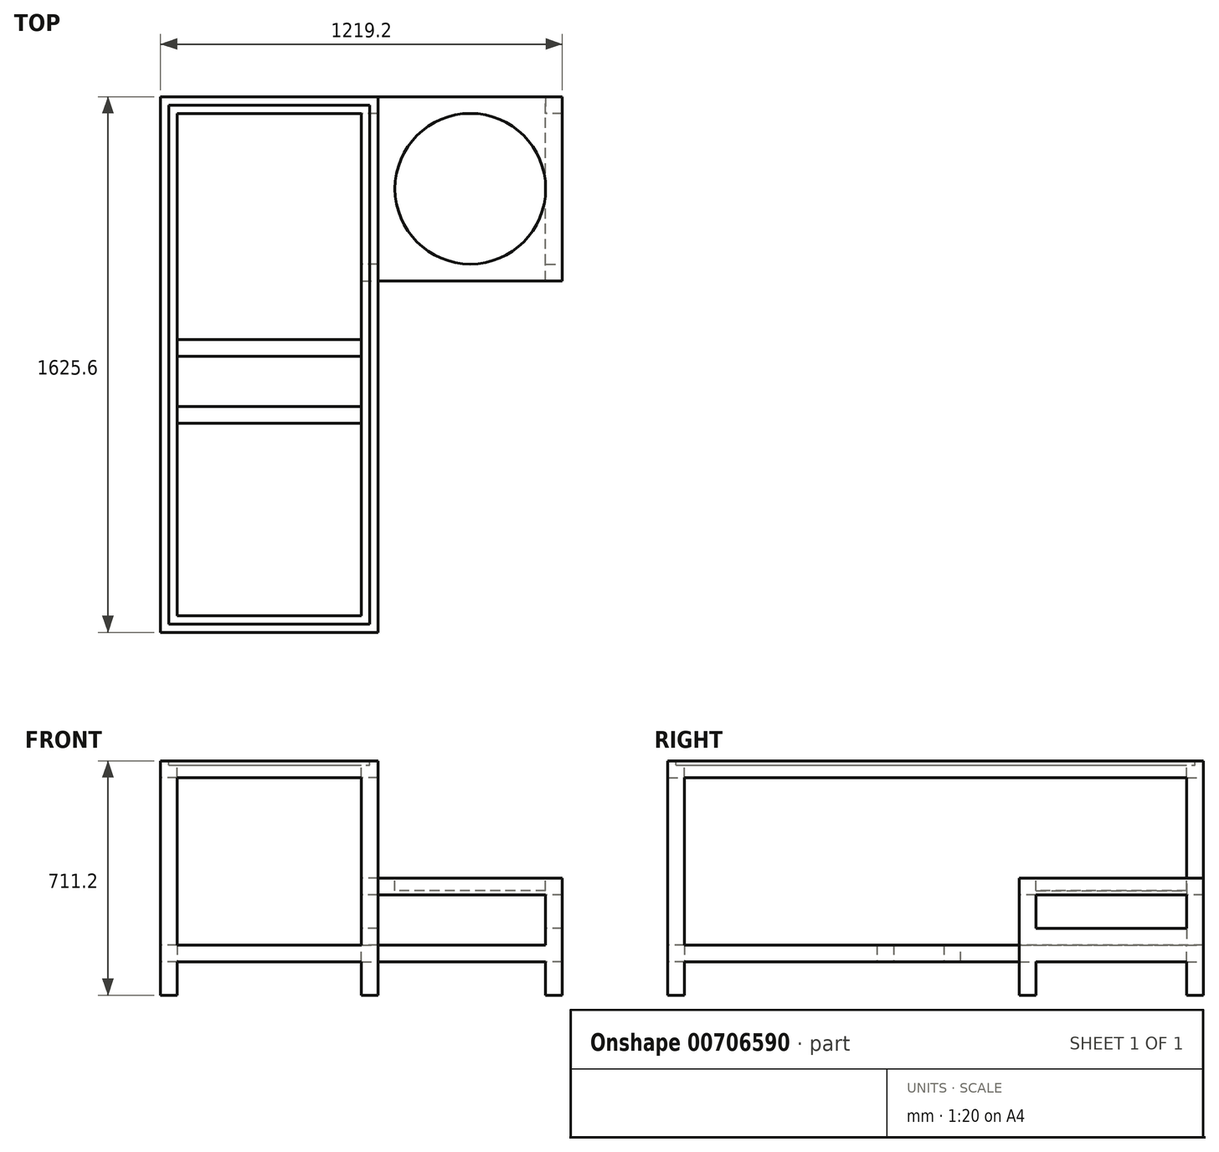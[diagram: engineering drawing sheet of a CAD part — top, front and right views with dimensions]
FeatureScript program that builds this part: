
annotation { "Feature Type Name" : "Feature", "Feature Type Description" : "" }
export const myFeature = defineFeature(function(context is Context, id is Id, definition is map)
    precondition{}
    {
        {
            var Q0;
            Q0=qCreatedBy(makeId("Top.planeOp"),FACE);
            var sketch = newSketch(context, id + "F0", { "sketchPlane" : qUnion([Q0])});
            skLineSegment(sketch, "E0.bottom", {"start": v(-609.6, -762) * mm, "end": v(609.6, -762) * mm});
            skLineSegment(sketch, "E0.top", {"start": v(-609.6, 762) * mm, "end": v(609.6, 762) * mm});
            skLineSegment(sketch, "E0.left", {"start": v(-609.6, -762) * mm, "end": v(-609.6, 762) * mm});
            skLineSegment(sketch, "E0.right", {"start": v(609.6, -762) * mm, "end": v(609.6, 762) * mm});
            skPoint(sketch, "E0.middle", {"position": v(0, 0) * mm});
            skLineSegment(sketch, "E1.0", {"start": v(660.4, -812.8) * mm, "end": v(660.4, 812.8) * mm});
            skLineSegment(sketch, "E1.1", {"start": v(-660.4, -812.8) * mm, "end": v(660.4, -812.8) * mm});
            skLineSegment(sketch, "E1.2", {"start": v(-660.4, -812.8) * mm, "end": v(-660.4, 812.8) * mm});
            skLineSegment(sketch, "E1.3", {"start": v(-660.4, 812.8) * mm, "end": v(660.4, 812.8) * mm});
            skSolve(sketch);
        }
        {
            var Q0;
            Q0=makeQuery(id+"F0.imprint","IMPRINT",FACE,{"disambiguationData":[TD([[makeQuery(id+"F0.imprint","IMPRINT",EDGE,{"derivedFrom":sQuery(id+"F0.wireOp",EDGE,"E0.bottom")}),-1.0]])]});
            extrude(context, id + "F1", {"entities" : qUnion([Q0]), "depth" : 50.8 * mm, "offsetDistance" : 25.4 * mm});
        }
        {
            var Q0;
            Q0=makeQuery(id+"F1.opExtrude","CAP_FACE",FACE,{"disambiguationData":[OSD([sQuery(id+"F0.wireOp",EDGE,"E0.bottom"),sQuery(id+"F0.wireOp",EDGE,"E0.top"),sQuery(id+"F0.wireOp",EDGE,"E0.left"),sQuery(id+"F0.wireOp",EDGE,"E0.right"),sQuery(id+"F0.wireOp",EDGE,"E1.0"),sQuery(id+"F0.wireOp",EDGE,"E1.1"),sQuery(id+"F0.wireOp",EDGE,"E1.2"),sQuery(id+"F0.wireOp",EDGE,"E1.3")])],"isStart":false});
            var sketch = newSketch(context, id + "F2", { "sketchPlane" : qUnion([Q0])});
            skLineSegment(sketch, "E2", {"start": v(-660.4, 812.8) * mm, "end": v(-609.6, 812.8) * mm});
            skLineSegment(sketch, "E3", {"start": v(-609.6, 812.8) * mm, "end": v(-609.6, 762) * mm});
            skLineSegment(sketch, "E4", {"start": v(-609.6, 762) * mm, "end": v(-660.4, 762) * mm});
            skLineSegment(sketch, "E5", {"start": v(-660.4, 762) * mm, "end": v(-660.4, 812.8) * mm});
            skLineSegment(sketch, "E6.MirrorCS", {"start": v(660.4, 812.8) * mm, "end": v(609.6, 812.8) * mm});
            skLineSegment(sketch, "E7.MirrorCS", {"start": v(609.6, 812.8) * mm, "end": v(609.6, 762) * mm});
            skLineSegment(sketch, "E8.MirrorCS", {"start": v(660.4, 762) * mm, "end": v(660.4, 812.8) * mm});
            skLineSegment(sketch, "E9.MirrorCS", {"start": v(609.6, 762) * mm, "end": v(660.4, 762) * mm});
            skLineSegment(sketch, "E10.MirrorCS", {"start": v(609.6, -762) * mm, "end": v(660.4, -762) * mm});
            skLineSegment(sketch, "E11.MirrorCS", {"start": v(-660.4, -812.8) * mm, "end": v(-609.6, -812.8) * mm});
            skLineSegment(sketch, "E12.MirrorCS", {"start": v(-609.6, -812.8) * mm, "end": v(-609.6, -762) * mm});
            skLineSegment(sketch, "E13.MirrorCS", {"start": v(660.4, -762) * mm, "end": v(660.4, -812.8) * mm});
            skLineSegment(sketch, "E14.MirrorCS", {"start": v(-609.6, -762) * mm, "end": v(-660.4, -762) * mm});
            skLineSegment(sketch, "E15.MirrorCS", {"start": v(609.6, -812.8) * mm, "end": v(609.6, -762) * mm});
            skLineSegment(sketch, "E16.MirrorCS", {"start": v(660.4, -812.8) * mm, "end": v(609.6, -812.8) * mm});
            skLineSegment(sketch, "E17.MirrorCS", {"start": v(-660.4, -762) * mm, "end": v(-660.4, -812.8) * mm});
            skSolve(sketch);
        }
        {
            var Q0;
            Q0 = qSketchRegion(id + "F2", true);
            extrude(context, id + "F3", {"entities" : qUnion([Q0]), "operationType" : NewBodyOperationType.ADD, "depth" : 508 * mm, "offsetDistance" : 25.4 * mm});
        }
        {
            var Q0;
            Q0=makeQuery(id+"F3.opExtrude","CAP_FACE",FACE,{"disambiguationData":[OSD([sQuery(id+"F2.wireOp",EDGE,"E2"),sQuery(id+"F2.wireOp",EDGE,"E3"),sQuery(id+"F2.wireOp",EDGE,"E4"),sQuery(id+"F2.wireOp",EDGE,"E5")])],"isStart":false});
            var sketch = newSketch(context, id + "F4", { "sketchPlane" : qUnion([Q0])});
            skLineSegment(sketch, "E18.bottom", {"start": v(-609.6, -762) * mm, "end": v(609.6, -762) * mm});
            skLineSegment(sketch, "E18.top", {"start": v(-609.6, 762) * mm, "end": v(609.6, 762) * mm});
            skLineSegment(sketch, "E18.left", {"start": v(-609.6, -762) * mm, "end": v(-609.6, 762) * mm});
            skLineSegment(sketch, "E18.right", {"start": v(609.6, -762) * mm, "end": v(609.6, 762) * mm});
            skPoint(sketch, "E18.middle", {"position": v(0, 0) * mm});
            skLineSegment(sketch, "E19.0", {"start": v(-660.4, -812.8) * mm, "end": v(660.4, -812.8) * mm});
            skLineSegment(sketch, "E19.1", {"start": v(-660.4, -812.8) * mm, "end": v(-660.4, 812.8) * mm});
            skLineSegment(sketch, "E19.2", {"start": v(-660.4, 812.8) * mm, "end": v(660.4, 812.8) * mm});
            skLineSegment(sketch, "E19.3", {"start": v(660.4, -812.8) * mm, "end": v(660.4, 812.8) * mm});
            skSolve(sketch);
        }
        {
            var Q0;
            Q0 = qSketchRegion(id + "F4", true);
            extrude(context, id + "F5", {"entities" : qUnion([Q0]), "operationType" : NewBodyOperationType.ADD, "depth" : 50.8 * mm, "offsetDistance" : 25.4 * mm});
        }
        {
            var Q0;
            Q0=makeQuery(id+"F5.opExtrude","SWEPT_FACE",FACE,{"disambiguationData":[OSD([sQuery(id+"F4.wireOp",EDGE,"E18.top")])]});
            var sketch = newSketch(context, id + "F6", { "sketchPlane" : qUnion([Q0])});
            skLineSegment(sketch, "E20", {"start": v(-609.6, 558.8) * mm, "end": v(-609.6, 609.6) * mm});
            skLineSegment(sketch, "E21", {"start": v(-609.6, 609.6) * mm, "end": v(0, 609.6) * mm});
            skLineSegment(sketch, "E22", {"start": v(0, 609.6) * mm, "end": v(0, 558.8) * mm});
            skLineSegment(sketch, "E23", {"start": v(0, 558.8) * mm, "end": v(-609.6, 558.8) * mm});
            skSolve(sketch);
        }
        {
            var Q0;
            Q0 = qSketchRegion(id + "F6", true);
            extrude(context, id + "F7", {"entities" : qUnion([Q0]), "operationType" : NewBodyOperationType.ADD, "endBound" : BoundingType.UP_TO_NEXT, "depth" : 25.4 * mm, "offsetDistance" : 25.4 * mm});
        }
        {
            var Q0;
            Q0=makeQuery(id+"F7.boolean.opBoolean","MERGE",FACE,{"derivedFrom":[makeQuery(id+"F5.opExtrude","CAP_FACE",FACE,{"disambiguationData":[OSD([sQuery(id+"F4.wireOp",EDGE,"E18.bottom"),sQuery(id+"F4.wireOp",EDGE,"E18.top"),sQuery(id+"F4.wireOp",EDGE,"E18.left"),sQuery(id+"F4.wireOp",EDGE,"E18.right"),sQuery(id+"F4.wireOp",EDGE,"E19.0"),sQuery(id+"F4.wireOp",EDGE,"E19.1"),sQuery(id+"F4.wireOp",EDGE,"E19.2"),sQuery(id+"F4.wireOp",EDGE,"E19.3")])],"isStart":false}),makeQuery(id+"F7.opExtrude","SWEPT_FACE",FACE,{"disambiguationData":[OSD([sQuery(id+"F6.wireOp",EDGE,"E21")])]})]});
            var sketch = newSketch(context, id + "F8", { "sketchPlane" : qUnion([Q0])});
            skLineSegment(sketch, "E24", {"start": v(0, 762) * mm, "end": v(0, 812.8) * mm});
            skLineSegment(sketch, "E25", {"start": v(0, 812.8) * mm, "end": v(660.4, 812.8) * mm});
            skLineSegment(sketch, "E26", {"start": v(660.4, 812.8) * mm, "end": v(660.4, -812.8) * mm});
            skLineSegment(sketch, "E27", {"start": v(660.4, -812.8) * mm, "end": v(0, -812.8) * mm});
            skLineSegment(sketch, "E28", {"start": v(0, -812.8) * mm, "end": v(0, 762) * mm});
            skSolve(sketch);
        }
        {
            var Q0;
            Q0 = qSketchRegion(id + "F8", true);
            extrude(context, id + "F9", {"entities" : qUnion([Q0]), "operationType" : NewBodyOperationType.REMOVE, "endBound" : BoundingType.THROUGH_ALL, "oppositeDirection" : true, "depth" : 25.4 * mm, "offsetDistance" : 25.4 * mm});
        }
        {
            var Q0;
            {var subQ0=sQuery(id+"F0.wireOp",EDGE,"E0.left");var subQ1=sQuery(id+"F0.wireOp",EDGE,"E1.3");var subQ2=sQuery(id+"F0.wireOp",EDGE,"E0.right");var subQ3=sQuery(id+"F0.wireOp",EDGE,"E0.top");var subQ4=makeQuery(id+"F1.opExtrude","CAP_FACE",FACE,{"disambiguationData":[OSD([sQuery(id+"F0.wireOp",EDGE,"E0.bottom"),subQ3,subQ0,subQ2,sQuery(id+"F0.wireOp",EDGE,"E1.0"),sQuery(id+"F0.wireOp",EDGE,"E1.1"),sQuery(id+"F0.wireOp",EDGE,"E1.2"),subQ1])],"isStart":false});Q0=makeQuery(id+"F3.boolean.opBoolean","SPLIT",FACE,{"disambiguationData":[TD([makeQuery(id+"F1.opExtrude","SWEPT_FACE",FACE,{"disambiguationData":[OSD([subQ1])]})])],"derivedFrom":subQ4});}
            var sketch = newSketch(context, id + "F10", { "sketchPlane" : qUnion([Q0])});
            skLineSegment(sketch, "E29", {"start": v(0, 812.8) * mm, "end": v(0, 762) * mm});
            skLineSegment(sketch, "E30", {"start": v(0, 762) * mm, "end": v(-50.8, 762) * mm});
            skLineSegment(sketch, "E31", {"start": v(-50.8, 762) * mm, "end": v(-50.8, 812.8) * mm});
            skLineSegment(sketch, "E32", {"start": v(-50.8, 812.8) * mm, "end": v(0, 812.8) * mm});
            skLineSegment(sketch, "E33.MirrorCS", {"start": v(-50.8, -812.8) * mm, "end": v(0, -812.8) * mm});
            skLineSegment(sketch, "E34.MirrorCS", {"start": v(0, -812.8) * mm, "end": v(0, -762) * mm});
            skLineSegment(sketch, "E35.MirrorCS", {"start": v(0, -762) * mm, "end": v(-50.8, -762) * mm});
            skLineSegment(sketch, "E36.MirrorCS", {"start": v(-50.8, -762) * mm, "end": v(-50.8, -812.8) * mm});
            skSolve(sketch);
        }
        {
            var Q0;
            Q0 = qSketchRegion(id + "F10", true);
            extrude(context, id + "F11", {"entities" : qUnion([Q0]), "operationType" : NewBodyOperationType.ADD, "endBound" : BoundingType.UP_TO_NEXT, "depth" : 25.4 * mm, "offsetDistance" : 25.4 * mm});
        }
        {
            var Q0;
            Q0=makeQuery(id+"F11.boolean.opBoolean","MERGE",FACE,{"derivedFrom":[makeQuery(id+"F1.opExtrude","SWEPT_FACE",FACE,{"disambiguationData":[OSD([sQuery(id+"F0.wireOp",EDGE,"E0.top")])]}),makeQuery(id+"F11.opExtrude","SWEPT_FACE",FACE,{"disambiguationData":[OSD([sQuery(id+"F10.wireOp",EDGE,"E30")])]})]});
            var sketch = newSketch(context, id + "F12", { "sketchPlane" : qUnion([Q0])});
            skLineSegment(sketch, "E37", {"start": v(-50.8, 50.8) * mm, "end": v(0, 50.8) * mm});
            skLineSegment(sketch, "E38", {"start": v(0, 50.8) * mm, "end": v(0, 0) * mm});
            skLineSegment(sketch, "E39", {"start": v(0, 0) * mm, "end": v(-50.8, 0) * mm});
            skLineSegment(sketch, "E40", {"start": v(-50.8, 0) * mm, "end": v(-50.8, 50.8) * mm});
            skSolve(sketch);
        }
        {
            var Q0;
            Q0 = qSketchRegion(id + "F12", true);
            extrude(context, id + "F13", {"entities" : qUnion([Q0]), "operationType" : NewBodyOperationType.ADD, "endBound" : BoundingType.UP_TO_NEXT, "depth" : 25.4 * mm, "offsetDistance" : 25.4 * mm});
        }
        {
            var Q0;
            {var subQ1=sQuery(id+"F0.wireOp",EDGE,"E0.top");var subQ7=sQuery(id+"F0.wireOp",EDGE,"E0.bottom");var subQ10=makeQuery(id+"F9.opExtrude","SWEPT_FACE",FACE,{"disambiguationData":[OSD([sQuery(id+"F8.wireOp",EDGE,"E24"),sQuery(id+"F8.wireOp",EDGE,"E28")])]});Q0=makeQuery(id+"F13.boolean.opBoolean","MERGE",FACE,{"derivedFrom":[makeQuery(id+"F11.boolean.opBoolean","MERGE",FACE,{"derivedFrom":[makeQuery(id+"F9.boolean.opBoolean","MERGE",FACE,{"derivedFrom":[makeQuery(id+"F7.opExtrude","SWEPT_FACE",FACE,{"disambiguationData":[OSD([sQuery(id+"F6.wireOp",EDGE,"E22")])]}),subQ10]}),makeQuery(id+"F9.boolean.opBoolean","COPY",FACE,{"disambiguationData":[TD([makeQuery(id+"F1.opExtrude","SWEPT_FACE",FACE,{"disambiguationData":[OSD([subQ7])]})])],"derivedFrom":subQ10}),makeQuery(id+"F9.boolean.opBoolean","COPY",FACE,{"disambiguationData":[TD([makeQuery(id+"F1.opExtrude","SWEPT_FACE",FACE,{"disambiguationData":[OSD([subQ1])]})])],"derivedFrom":subQ10}),makeQuery(id+"F11.opExtrude","SWEPT_FACE",FACE,{"disambiguationData":[OSD([sQuery(id+"F10.wireOp",EDGE,"E29")])]}),makeQuery(id+"F11.opExtrude","SWEPT_FACE",FACE,{"disambiguationData":[OSD([sQuery(id+"F10.wireOp",EDGE,"E34.MirrorCS")])]})]}),makeQuery(id+"F13.opExtrude","SWEPT_FACE",FACE,{"disambiguationData":[OSD([sQuery(id+"F12.wireOp",EDGE,"E38")])]})]});}
            var sketch = newSketch(context, id + "F14", { "sketchPlane" : qUnion([Q0])});
            skLineSegment(sketch, "E41", {"start": v(812.8, 0) * mm, "end": v(254, 0) * mm});
            skLineSegment(sketch, "E42", {"start": v(254, 0) * mm, "end": v(254, 254) * mm});
            skLineSegment(sketch, "E43", {"start": v(254, 254) * mm, "end": v(812.8, 254) * mm});
            skLineSegment(sketch, "E44", {"start": v(812.8, 254) * mm, "end": v(812.8, 0) * mm});
            skSolve(sketch);
        }
        {
            var Q0;
            Q0 = qSketchRegion(id + "F14", true);
            extrude(context, id + "F15", {"entities" : qUnion([Q0]), "operationType" : NewBodyOperationType.ADD, "depth" : 558.8 * mm, "offsetDistance" : 25.4 * mm});
        }
        {
            var Q0;
            Q0=makeQuery(id+"F15.opExtrude","CAP_FACE",FACE,{"disambiguationData":[OSD([sQuery(id+"F14.wireOp",EDGE,"E41"),sQuery(id+"F14.wireOp",EDGE,"E42"),sQuery(id+"F14.wireOp",EDGE,"E43"),sQuery(id+"F14.wireOp",EDGE,"E44")])],"isStart":true});
            extrude(context, id + "F16", {"entities" : qUnion([Q0]), "operationType" : NewBodyOperationType.ADD, "depth" : 50.8 * mm, "offsetDistance" : 25.4 * mm});
        }
        {
            var Q0;
            {var subQ0=sQuery(id+"F14.wireOp",EDGE,"E42");Q0=makeQuery(id+"F16.boolean.opBoolean","MERGE",FACE,{"derivedFrom":[makeQuery(id+"F15.opExtrude","SWEPT_FACE",FACE,{"disambiguationData":[OSD([subQ0])]}),makeQuery(id+"F16.opExtrude","SWEPT_FACE",FACE,{"disambiguationData":[OSD([subQ0])]})]});}
            var sketch = newSketch(context, id + "F17", { "sketchPlane" : qUnion([Q0])});
            skLineSegment(sketch, "E45.0", {"start": v(-0.63, 203.2) * mm, "end": v(508, 203.2) * mm});
            skLineSegment(sketch, "E45.1", {"start": v(-0.63, 50.8) * mm, "end": v(-0.63, 203.2) * mm});
            skLineSegment(sketch, "E45.2", {"start": v(508, 50.8) * mm, "end": v(-0.63, 50.8) * mm});
            skLineSegment(sketch, "E45.3", {"start": v(508, 203.2) * mm, "end": v(508, 50.8) * mm});
            skSolve(sketch);
        }
        {
            var Q0;
            Q0 = qSketchRegion(id + "F17", true);
            extrude(context, id + "F18", {"entities" : qUnion([Q0]), "operationType" : NewBodyOperationType.REMOVE, "endBound" : BoundingType.THROUGH_ALL, "oppositeDirection" : true, "depth" : 25.4 * mm, "offsetDistance" : 25.4 * mm});
        }
        {
            var Q0;
            Q0=makeQuery(id+"F16.boolean.opBoolean","MERGE",FACE,{"derivedFrom":[makeQuery(id+"F11.opExtrude","SWEPT_FACE",FACE,{"disambiguationData":[OSD([sQuery(id+"F10.wireOp",EDGE,"E31")])]}),makeQuery(id+"F13.opExtrude","SWEPT_FACE",FACE,{"disambiguationData":[OSD([sQuery(id+"F12.wireOp",EDGE,"E40")])]}),makeQuery(id+"F16.opExtrude","CAP_FACE",FACE,{"disambiguationData":[OSD([sQuery(id+"F14.wireOp",EDGE,"E41"),sQuery(id+"F14.wireOp",EDGE,"E42"),sQuery(id+"F14.wireOp",EDGE,"E43"),sQuery(id+"F14.wireOp",EDGE,"E44")])],"isStart":false})]});
            var sketch = newSketch(context, id + "F19", { "sketchPlane" : qUnion([Q0])});
            skLineSegment(sketch, "E46.0", {"start": v(-761.94, 101.6) * mm, "end": v(-761.94, 203.2) * mm});
            skLineSegment(sketch, "E46.1", {"start": v(-304.8, 101.6) * mm, "end": v(-761.94, 101.6) * mm});
            skLineSegment(sketch, "E46.2", {"start": v(-304.8, 203.2) * mm, "end": v(-304.8, 101.6) * mm});
            skLineSegment(sketch, "E46.3", {"start": v(-761.94, 203.2) * mm, "end": v(-304.8, 203.2) * mm});
            skSolve(sketch);
        }
        {
            var Q0;
            Q0 = qSketchRegion(id + "F19", true);
            extrude(context, id + "F20", {"entities" : qUnion([Q0]), "operationType" : NewBodyOperationType.REMOVE, "endBound" : BoundingType.THROUGH_ALL, "oppositeDirection" : true, "depth" : 25.4 * mm, "offsetDistance" : 25.4 * mm});
        }
        {
            var Q0;
            Q0=makeQuery(id+"F7.boolean.opBoolean","MERGE",FACE,{"derivedFrom":[makeQuery(id+"F5.opExtrude","CAP_FACE",FACE,{"disambiguationData":[OSD([sQuery(id+"F4.wireOp",EDGE,"E18.bottom"),sQuery(id+"F4.wireOp",EDGE,"E18.top"),sQuery(id+"F4.wireOp",EDGE,"E18.left"),sQuery(id+"F4.wireOp",EDGE,"E18.right"),sQuery(id+"F4.wireOp",EDGE,"E19.0"),sQuery(id+"F4.wireOp",EDGE,"E19.1"),sQuery(id+"F4.wireOp",EDGE,"E19.2"),sQuery(id+"F4.wireOp",EDGE,"E19.3")])],"isStart":false}),makeQuery(id+"F7.opExtrude","SWEPT_FACE",FACE,{"disambiguationData":[OSD([sQuery(id+"F6.wireOp",EDGE,"E21")])]})]});
            var sketch = newSketch(context, id + "F21", { "sketchPlane" : qUnion([Q0])});
            skLineSegment(sketch, "E47.0", {"start": v(-635, -787.4) * mm, "end": v(-635, 787.4) * mm});
            skLineSegment(sketch, "E47.1", {"start": v(-635, -787.4) * mm, "end": v(-25.4, -787.4) * mm});
            skLineSegment(sketch, "E47.2", {"start": v(-25.4, -787.4) * mm, "end": v(-25.4, 787.4) * mm});
            skLineSegment(sketch, "E47.3", {"start": v(-635, 787.4) * mm, "end": v(-25.4, 787.4) * mm});
            skSolve(sketch);
        }
        {
            var Q0;
            Q0 = qSketchRegion(id + "F21", true);
            extrude(context, id + "F22", {"entities" : qUnion([Q0]), "operationType" : NewBodyOperationType.REMOVE, "oppositeDirection" : true, "depth" : 12.7 * mm, "offsetDistance" : 25.4 * mm});
        }
        {
            var Q0;
            Q0=makeQuery(id+"F22.boolean.opBoolean","COPY",FACE,{"derivedFrom":makeQuery(id+"F22.opExtrude","CAP_FACE",FACE,{"disambiguationData":[OSD([sQuery(id+"F21.wireOp",EDGE,"E47.0"),sQuery(id+"F21.wireOp",EDGE,"E47.1"),sQuery(id+"F21.wireOp",EDGE,"E47.2"),sQuery(id+"F21.wireOp",EDGE,"E47.3")])],"isStart":false})});
            var sketch = newSketch(context, id + "F23", { "sketchPlane" : qUnion([Q0])});
            skLineSegment(sketch, "E48.3", {"start": v(-635, -787.4) * mm, "end": v(-25.4, -787.4) * mm});
            skLineSegment(sketch, "E49.0", {"start": v(-609.6, -762) * mm, "end": v(-609.6, 762) * mm});
            skLineSegment(sketch, "E49.1", {"start": v(-609.6, -762) * mm, "end": v(-50.8, -762) * mm});
            skLineSegment(sketch, "E49.2", {"start": v(-50.8, -762) * mm, "end": v(-50.8, 762) * mm});
            skLineSegment(sketch, "E49.3", {"start": v(-609.6, 762) * mm, "end": v(-50.8, 762) * mm});
            skSolve(sketch);
        }
        {
            var Q0;
            Q0 = qSketchRegion(id + "F23", true);
            extrude(context, id + "F24", {"entities" : qUnion([Q0]), "operationType" : NewBodyOperationType.REMOVE, "endBound" : BoundingType.THROUGH_ALL, "oppositeDirection" : true, "depth" : 25.4 * mm, "offsetDistance" : 25.4 * mm});
        }
        {
            var Q0;
            Q0=makeQuery(id+"F15.boolean.opBoolean","MERGE",FACE,{"derivedFrom":[makeQuery(id+"F13.boolean.opBoolean","MERGE",FACE,{"derivedFrom":[makeQuery(id+"F1.opExtrude","CAP_FACE",FACE,{"disambiguationData":[OSD([sQuery(id+"F0.wireOp",EDGE,"E0.bottom"),sQuery(id+"F0.wireOp",EDGE,"E0.top"),sQuery(id+"F0.wireOp",EDGE,"E0.left"),sQuery(id+"F0.wireOp",EDGE,"E0.right"),sQuery(id+"F0.wireOp",EDGE,"E1.0"),sQuery(id+"F0.wireOp",EDGE,"E1.1"),sQuery(id+"F0.wireOp",EDGE,"E1.2"),sQuery(id+"F0.wireOp",EDGE,"E1.3")])],"isStart":true}),makeQuery(id+"F13.opExtrude","SWEPT_FACE",FACE,{"disambiguationData":[OSD([sQuery(id+"F12.wireOp",EDGE,"E39")])]})]}),makeQuery(id+"F15.opExtrude","SWEPT_FACE",FACE,{"disambiguationData":[OSD([sQuery(id+"F14.wireOp",EDGE,"E41")])]})]});
            var sketch = newSketch(context, id + "F25", { "sketchPlane" : qUnion([Q0])});
            skLineSegment(sketch, "E50", {"start": v(-609.6, 762) * mm, "end": v(-660.4, 762) * mm});
            skLineSegment(sketch, "E51", {"start": v(-660.4, 762) * mm, "end": v(-660.4, 812.8) * mm});
            skLineSegment(sketch, "E52", {"start": v(-660.4, 812.8) * mm, "end": v(-609.6, 812.8) * mm});
            skLineSegment(sketch, "E53", {"start": v(-609.6, 812.8) * mm, "end": v(-609.6, 762) * mm});
            skLineSegment(sketch, "E54", {"start": v(-50.8, 762) * mm, "end": v(-50.8, 812.8) * mm});
            skLineSegment(sketch, "E55", {"start": v(-50.8, 812.8) * mm, "end": v(0, 812.8) * mm});
            skLineSegment(sketch, "E56", {"start": v(0, 812.8) * mm, "end": v(0, 762) * mm});
            skLineSegment(sketch, "E57", {"start": v(0, 762) * mm, "end": v(-50.8, 762) * mm});
            skLineSegment(sketch, "E58.MirrorCS", {"start": v(-609.6, -762) * mm, "end": v(-660.4, -762) * mm});
            skLineSegment(sketch, "E59.MirrorCS", {"start": v(-660.4, -762) * mm, "end": v(-660.4, -812.8) * mm});
            skLineSegment(sketch, "E60.MirrorCS", {"start": v(-609.6, -812.8) * mm, "end": v(-609.6, -762) * mm});
            skLineSegment(sketch, "E61.MirrorCS", {"start": v(-50.8, -762) * mm, "end": v(-50.8, -812.8) * mm});
            skLineSegment(sketch, "E62.MirrorCS", {"start": v(-50.8, -812.8) * mm, "end": v(0, -812.8) * mm});
            skLineSegment(sketch, "E63.MirrorCS", {"start": v(0, -762) * mm, "end": v(-50.8, -762) * mm});
            skLineSegment(sketch, "E64.MirrorCS", {"start": v(0, -812.8) * mm, "end": v(0, -762) * mm});
            skLineSegment(sketch, "E65.MirrorCS", {"start": v(-660.4, -812.8) * mm, "end": v(-609.6, -812.8) * mm});
            skLineSegment(sketch, "E66", {"start": v(0, -254) * mm, "end": v(-50.8, -254) * mm});
            skLineSegment(sketch, "E67", {"start": v(-50.8, -254) * mm, "end": v(-50.8, -304.8) * mm});
            skLineSegment(sketch, "E68", {"start": v(-50.8, -304.8) * mm, "end": v(0, -304.8) * mm});
            skLineSegment(sketch, "E69", {"start": v(0, -304.8) * mm, "end": v(0, -254) * mm});
            skLineSegment(sketch, "E70", {"start": v(558.8, -254) * mm, "end": v(508, -254) * mm});
            skLineSegment(sketch, "E71", {"start": v(508, -254) * mm, "end": v(508, -304.8) * mm});
            skLineSegment(sketch, "E72", {"start": v(508, -304.8) * mm, "end": v(558.8, -304.8) * mm});
            skLineSegment(sketch, "E73", {"start": v(558.8, -304.8) * mm, "end": v(558.8, -254) * mm});
            skLineSegment(sketch, "E74", {"start": v(558.8, -812.8) * mm, "end": v(558.8, -762) * mm});
            skLineSegment(sketch, "E75", {"start": v(558.8, -762) * mm, "end": v(508, -762) * mm});
            skLineSegment(sketch, "E76", {"start": v(508, -762) * mm, "end": v(508, -812.8) * mm});
            skLineSegment(sketch, "E77", {"start": v(508, -812.8) * mm, "end": v(558.8, -812.8) * mm});
            skSolve(sketch);
        }
        {
            var Q0;
            Q0 = qSketchRegion(id + "F25", true);
            extrude(context, id + "F26", {"entities" : qUnion([Q0]), "operationType" : NewBodyOperationType.ADD, "depth" : 101.6 * mm, "offsetDistance" : 25.4 * mm});
        }
        {
            var Q0;
            Q0=makeQuery(id+"F1.opExtrude","SWEPT_FACE",FACE,{"disambiguationData":[OSD([sQuery(id+"F0.wireOp",EDGE,"E0.left")])]});
            var sketch = newSketch(context, id + "F27", { "sketchPlane" : qUnion([Q0])});
            skLineSegment(sketch, "E78.0", {"start": v(-177.8, 50.8) * mm, "end": v(-177.8, 0) * mm});
            skLineSegment(sketch, "E79.0", {"start": v(-127, 50.8) * mm, "end": v(-127, 0) * mm});
            skLineSegment(sketch, "E80.0", {"start": v(25.4, 50.8) * mm, "end": v(25.4, 0) * mm});
            skLineSegment(sketch, "E81.0", {"start": v(76.2, 50.8) * mm, "end": v(76.2, 0) * mm});
            skLineSegment(sketch, "E82.trimOffspring", {"start": v(25.4, 0) * mm, "end": v(76.2, 0) * mm});
            skLineSegment(sketch, "E83.trimOffspring", {"start": v(25.4, 50.8) * mm, "end": v(76.2, 50.8) * mm});
            skPoint(sketch, "E84.orphan", {"position": v(254, 50.8) * mm});
            skPoint(sketch, "E85.orphan", {"position": v(254, 0) * mm});
            skLineSegment(sketch, "E86.trimOffspring", {"start": v(-177.8, 0) * mm, "end": v(-127, 0) * mm});
            skLineSegment(sketch, "E87.trimOffspring", {"start": v(-177.8, 50.8) * mm, "end": v(-127, 50.8) * mm});
            skPoint(sketch, "E88.0.start.orphan", {"position": v(-762, 50.8) * mm});
            skPoint(sketch, "E88.2.end.orphan", {"position": v(-762, 0) * mm});
            skPoint(sketch, "E88.2.start.orphan", {"position": v(-762, 50.8) * mm});
            skPoint(sketch, "E88.1.start.orphan", {"position": v(-762, 0) * mm});
            skSolve(sketch);
        }
        {
            var Q0;
            Q0 = qSketchRegion(id + "F27", true);
            extrude(context, id + "F28", {"entities" : qUnion([Q0]), "operationType" : NewBodyOperationType.ADD, "endBound" : BoundingType.UP_TO_NEXT, "depth" : 25.4 * mm, "offsetDistance" : 25.4 * mm});
        }
        {
            var Q0;
            {var subQ0=sQuery(id+"F14.wireOp",EDGE,"E43");Q0=makeQuery(id+"F16.boolean.opBoolean","MERGE",FACE,{"derivedFrom":[makeQuery(id+"F15.opExtrude","SWEPT_FACE",FACE,{"disambiguationData":[OSD([subQ0])]}),makeQuery(id+"F16.opExtrude","SWEPT_FACE",FACE,{"disambiguationData":[OSD([subQ0])]})]});}
            var sketch = newSketch(context, id + "F29", { "sketchPlane" : qUnion([Q0])});
            skPoint(sketch, "E89", {"position": v(279.4, 533.4) * mm});
            skCircle(sketch, "E90", {"center": v(279.4, 533.4) * mm, "radius": 228.6 * mm});
            skSolve(sketch);
        }
        {
            var Q0;
            Q0 = qSketchRegion(id + "F29", true);
            extrude(context, id + "F30", {"entities" : qUnion([Q0]), "operationType" : NewBodyOperationType.REMOVE, "oppositeDirection" : true, "depth" : 38.1 * mm, "offsetDistance" : 25.4 * mm});
        }
    });
